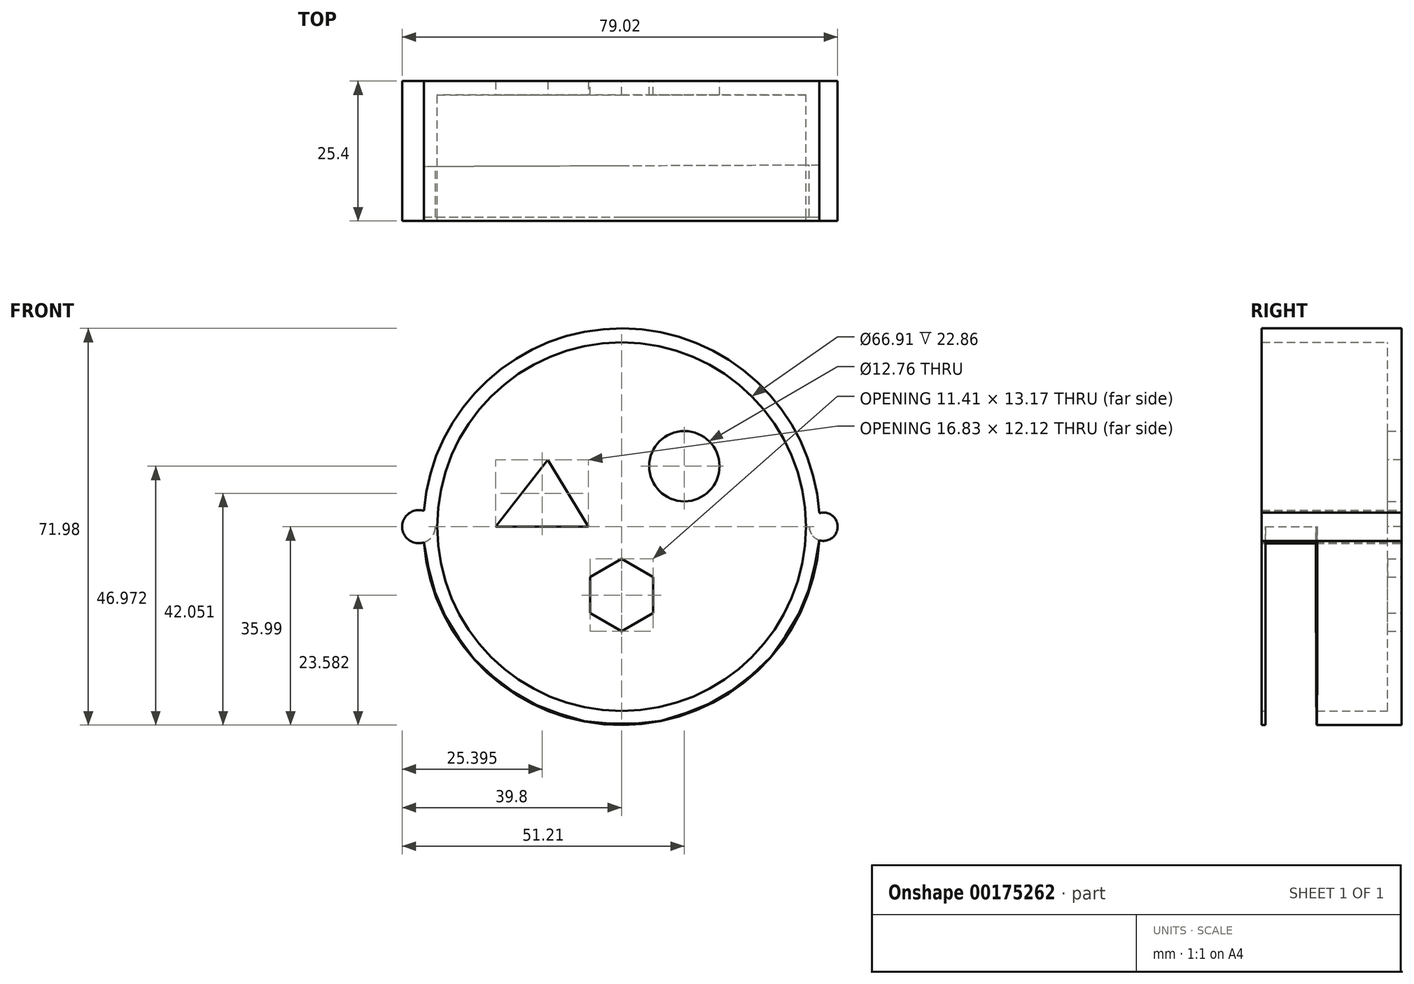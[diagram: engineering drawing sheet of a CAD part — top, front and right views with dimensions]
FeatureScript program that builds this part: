
annotation { "Feature Type Name" : "Feature", "Feature Type Description" : "" }
export const myFeature = defineFeature(function(context is Context, id is Id, definition is map)
    precondition{}
    {
        {
            var Q0;
            Q0=qCreatedBy(makeId("Front.planeOp"),FACE);
            var sketch = newSketch(context, id + "F0", { "sketchPlane" : qUnion([Q0])});
            skCircle(sketch, "E0", {"center": v(0, 0) * mm, "radius": 36 * mm});
            skSolve(sketch);
        }
        {
            var Q0;
            Q0 = qSketchRegion(id + "F0", true);
            extrude(context, id + "F1", {"entities" : qUnion([Q0]), "depth" : 25.4 * mm});
        }
        {
            var Q0;
            Q0=makeQuery(id+"F1.opExtrude","CAP_FACE",FACE,{"disambiguationData":[OSD([sQuery(id+"F0.wireOp",EDGE,"E0")])],"isStart":false});
            var sketch = newSketch(context, id + "F2", { "sketchPlane" : qUnion([Q0])});
            skCircle(sketch, "E1", {"center": v(0, 0) * mm, "radius": 31.13 * mm});
            skSolve(sketch);
        }
        {
            var Q0;
            Q0=makeQuery(id+"F1.opExtrude","CAP_FACE",FACE,{"disambiguationData":[OSD([sQuery(id+"F0.wireOp",EDGE,"E0")])],"isStart":false});
            shell(context, id + "F3", {"entities" : qUnion([Q0]), "thickness" : 2.54 * mm});
        }
        {
            var Q0;
            Q0=makeQuery(id+"F2.imprint","IMPRINT",FACE,{"disambiguationData":[TD([[makeQuery(id+"F2.imprint","IMPRINT",EDGE,{"derivedFrom":sQuery(id+"F2.wireOp",EDGE,"E1")}),1.0]])]});
            var sketch = newSketch(context, id + "F4", { "sketchPlane" : qUnion([Q0])});
            skLineSegment(sketch, "E2", {"start": v(-22.82, 0) * mm, "end": v(-13.4, 12.12) * mm});
            skLineSegment(sketch, "E3", {"start": v(-13.4, 12.12) * mm, "end": v(-6, 0) * mm});
            skLineSegment(sketch, "E4", {"start": v(-6, 0) * mm, "end": v(-22.82, 0) * mm});
            skSolve(sketch);
        }
        {
            var Q0;
            Q0 = qSketchRegion(id + "F4", true);
            extrude(context, id + "F5", {"entities" : qUnion([Q0]), "operationType" : NewBodyOperationType.REMOVE, "endBound" : BoundingType.THROUGH_ALL, "oppositeDirection" : true, "depth" : 25.4 * mm});
        }
        {
            var Q0;
            Q0=qCreatedBy(makeId("Front.planeOp"),FACE);
            var sketch = newSketch(context, id + "F6", { "sketchPlane" : qUnion([Q0])});
            skCircle(sketch, "E5", {"center": v(11.4, 10.98) * mm, "radius": 6.38 * mm});
            skSolve(sketch);
        }
        {
            var Q0;
            Q0 = qSketchRegion(id + "F6", true);
            var Q1;
            Q1=makeQuery(id+"F1.opExtrude","SWEPT_BODY",BODY,{"disambiguationData":[OSD([sQuery(id+"F0.wireOp",EDGE,"E0")])]});
            extrude(context, id + "F7", {"entities" : qUnion([Q0]), "operationType" : NewBodyOperationType.REMOVE, "endBound" : BoundingType.UP_TO_BODY, "endBoundEntityBody" : qUnion([Q1]), "depth" : 25.4 * mm});
        }
        {
            var Q0;
            Q0=qCreatedBy(makeId("Front.planeOp"),FACE);
            var sketch = newSketch(context, id + "F8", { "sketchPlane" : qUnion([Q0])});
            skCircle(sketch, "E6.cCircle", {"center": v(0, -14.69) * mm, "radius": 6.76 * mm, "construction": true});
            skLineSegment(sketch, "E6.0", {"start": v(4.18, -8.1) * mm, "end": v(7.8, -15.01) * mm});
            skLineSegment(sketch, "E6.1", {"start": v(7.8, -15.01) * mm, "end": v(3.62, -21.6) * mm});
            skLineSegment(sketch, "E6.2", {"start": v(3.62, -21.6) * mm, "end": v(-4.18, -21.29) * mm});
            skLineSegment(sketch, "E6.3", {"start": v(-4.18, -21.29) * mm, "end": v(-7.8, -14.37) * mm});
            skLineSegment(sketch, "E6.4", {"start": v(-7.8, -14.37) * mm, "end": v(-3.62, -7.77) * mm});
            skLineSegment(sketch, "E6.5", {"start": v(-3.62, -7.77) * mm, "end": v(4.18, -8.1) * mm});
            skPoint(sketch, "E6.0.midPoint", {"position": v(6, -11.55) * mm});
            skSolve(sketch);
        }
        {
            var Q0;
            Q0 = qSketchRegion(id + "F8", true);
            extrude(context, id + "F9", {"entities" : qUnion([Q0]), "operationType" : NewBodyOperationType.REMOVE, "endBound" : BoundingType.THROUGH_ALL, "oppositeDirection" : true, "depth" : 25.4 * mm});
        }
        {
            var Q0;
            Q0=qCreatedBy(makeId("Front.planeOp"),FACE);
            var sketch = newSketch(context, id + "F10", { "sketchPlane" : qUnion([Q0])});
            skLineSegment(sketch, "E7", {"start": v(0, -13.4) * mm, "end": v(-18.68, -13.4) * mm});
            skLineSegment(sketch, "E8", {"start": v(-18.68, -13.4) * mm, "end": v(-18.68, -6.85) * mm});
            skLineSegment(sketch, "E9", {"start": v(-18.68, -6.85) * mm, "end": v(0, -6.85) * mm});
            skLineSegment(sketch, "E10", {"start": v(0, -6.85) * mm, "end": v(0, -13.4) * mm});
            skSolve(sketch);
        }
        {
            var Q0;
            Q0 = qSketchRegion(id + "F10", true);
            extrude(context, id + "F11", {"entities" : qUnion([Q0]), "operationType" : NewBodyOperationType.REMOVE, "endBound" : BoundingType.THROUGH_ALL, "oppositeDirection" : true, "depth" : 25.4 * mm});
        }
        {
            var Q0;
            Q0=qCreatedBy(makeId("Front.planeOp"),FACE);
            var sketch = newSketch(context, id + "F12", { "sketchPlane" : qUnion([Q0])});
            skLineSegment(sketch, "E11", {"start": v(12.4, -20.25) * mm, "end": v(-16.4, -20.25) * mm});
            skLineSegment(sketch, "E12", {"start": v(-16.4, -20.25) * mm, "end": v(-16.4, -13.98) * mm});
            skLineSegment(sketch, "E13", {"start": v(-16.4, -13.98) * mm, "end": v(14.98, -13.98) * mm});
            skLineSegment(sketch, "E14", {"start": v(14.98, -13.98) * mm, "end": v(12.4, -20.25) * mm});
            skSolve(sketch);
        }
        {
            var Q0;
            Q0=makeQuery(id+"F12.imprint","IMPRINT",FACE,{"disambiguationData":[TD([[makeQuery(id+"F12.imprint","IMPRINT",EDGE,{"derivedFrom":sQuery(id+"F12.wireOp",EDGE,"E11")}),-1.0]])]});
            extrude(context, id + "F13", {"entities" : qUnion([Q0]), "operationType" : NewBodyOperationType.REMOVE, "endBound" : BoundingType.THROUGH_ALL, "oppositeDirection" : true, "depth" : 25.4 * mm});
        }
        {
            var Q0;
            Q0=qCreatedBy(makeId("Front.planeOp"),FACE);
            var sketch = newSketch(context, id + "F14", { "sketchPlane" : qUnion([Q0])});
            skCircle(sketch, "E15.cCircle", {"center": v(0, -14.69) * mm, "radius": 7.29 * mm, "construction": true});
            skLineSegment(sketch, "E15.0", {"start": v(4.13, -7.36) * mm, "end": v(8.42, -14.6) * mm});
            skLineSegment(sketch, "E15.1", {"start": v(8.42, -14.6) * mm, "end": v(4.28, -21.94) * mm});
            skLineSegment(sketch, "E15.2", {"start": v(4.28, -21.94) * mm, "end": v(-4.13, -22.02) * mm});
            skLineSegment(sketch, "E15.3", {"start": v(-4.13, -22.02) * mm, "end": v(-8.42, -14.77) * mm});
            skLineSegment(sketch, "E15.4", {"start": v(-8.42, -14.77) * mm, "end": v(-4.28, -7.44) * mm});
            skLineSegment(sketch, "E15.5", {"start": v(-4.28, -7.44) * mm, "end": v(4.13, -7.36) * mm});
            skPoint(sketch, "E15.0.midPoint", {"position": v(6.28, -10.98) * mm});
            skSolve(sketch);
        }
        {
            var Q0;
            Q0 = qSketchRegion(id + "F14", true);
            extrude(context, id + "F15", {"entities" : qUnion([Q0]), "operationType" : NewBodyOperationType.REMOVE, "endBound" : BoundingType.THROUGH_ALL, "oppositeDirection" : true, "depth" : 25.4 * mm});
        }
        {
            var Q0;
            Q0=qCreatedBy(makeId("Front.planeOp"),FACE);
            var sketch = newSketch(context, id + "F16", { "sketchPlane" : qUnion([Q0])});
            skCircle(sketch, "E16.cCircle", {"center": v(0, -12.4) * mm, "radius": 5.7 * mm, "construction": true});
            skLineSegment(sketch, "E16.0", {"start": v(5.7, -9.11) * mm, "end": v(5.7, -15.7) * mm});
            skLineSegment(sketch, "E16.1", {"start": v(5.7, -15.7) * mm, "end": v(0, -19) * mm});
            skLineSegment(sketch, "E16.2", {"start": v(0, -19) * mm, "end": v(-5.7, -15.7) * mm});
            skLineSegment(sketch, "E16.3", {"start": v(-5.7, -15.7) * mm, "end": v(-5.7, -9.11) * mm});
            skLineSegment(sketch, "E16.4", {"start": v(-5.7, -9.11) * mm, "end": v(0, -5.82) * mm});
            skLineSegment(sketch, "E16.5", {"start": v(0, -5.82) * mm, "end": v(5.7, -9.11) * mm});
            skPoint(sketch, "E16.0.midPoint", {"position": v(5.7, -12.4) * mm});
            skSolve(sketch);
        }
        {
            var Q0;
            Q0 = qSketchRegion(id + "F16", true);
            var Q1;
            Q1=makeQuery(id+"F1.opExtrude","SWEPT_BODY",BODY,{"disambiguationData":[OSD([sQuery(id+"F0.wireOp",EDGE,"E0")])]});
            extrude(context, id + "F17", {"entities" : qUnion([Q0]), "operationType" : NewBodyOperationType.REMOVE, "endBound" : BoundingType.THROUGH_ALL, "endBoundEntityBody" : qUnion([Q1]), "depth" : 25.4 * mm});
        }
        {
            var Q0;
            Q0=qCreatedBy(makeId("Top.planeOp"),FACE);
            var sketch = newSketch(context, id + "F18", { "sketchPlane" : qUnion([Q0])});
            skLineSegment(sketch, "E17", {"start": v(-36.8, -15.55) * mm, "end": v(-36.8, -24.67) * mm});
            skLineSegment(sketch, "E18", {"start": v(-36.8, -24.67) * mm, "end": v(39.36, -24.67) * mm});
            skLineSegment(sketch, "E19", {"start": v(39.36, -25.24) * mm, "end": v(39.36, -15.26) * mm});
            skLineSegment(sketch, "E20", {"start": v(39.36, -15.26) * mm, "end": v(-36.8, -15.55) * mm});
            skSolve(sketch);
        }
        {
            var Q0;
            Q0 = qSketchRegion(id + "F18", true);
            extrude(context, id + "F19", {"entities" : qUnion([Q0]), "operationType" : NewBodyOperationType.REMOVE, "endBound" : BoundingType.THROUGH_ALL, "oppositeDirection" : true, "depth" : 25.4 * mm});
        }
        {
            var Q0;
            Q0=qCreatedBy(makeId("Front.planeOp"),FACE);
            var sketch = newSketch(context, id + "F20", { "sketchPlane" : qUnion([Q0])});
            skCircle(sketch, "E21", {"center": v(-36.8, 0) * mm, "radius": 3 * mm});
            skSolve(sketch);
        }
        {
            var Q0;
            Q0 = qSketchRegion(id + "F20", true);
            extrude(context, id + "F21", {"entities" : qUnion([Q0]), "operationType" : NewBodyOperationType.ADD, "depth" : 25.4 * mm});
        }
        {
            var Q0;
            Q0=qCreatedBy(makeId("Front.planeOp"),FACE);
            var sketch = newSketch(context, id + "F22", { "sketchPlane" : qUnion([Q0])});
            skCircle(sketch, "E22", {"center": v(36.65, 0) * mm, "radius": 2.57 * mm});
            skSolve(sketch);
        }
        {
            var Q0;
            Q0 = qSketchRegion(id + "F22", true);
            extrude(context, id + "F23", {"entities" : qUnion([Q0]), "operationType" : NewBodyOperationType.ADD, "depth" : 25.4 * mm});
        }
    });
